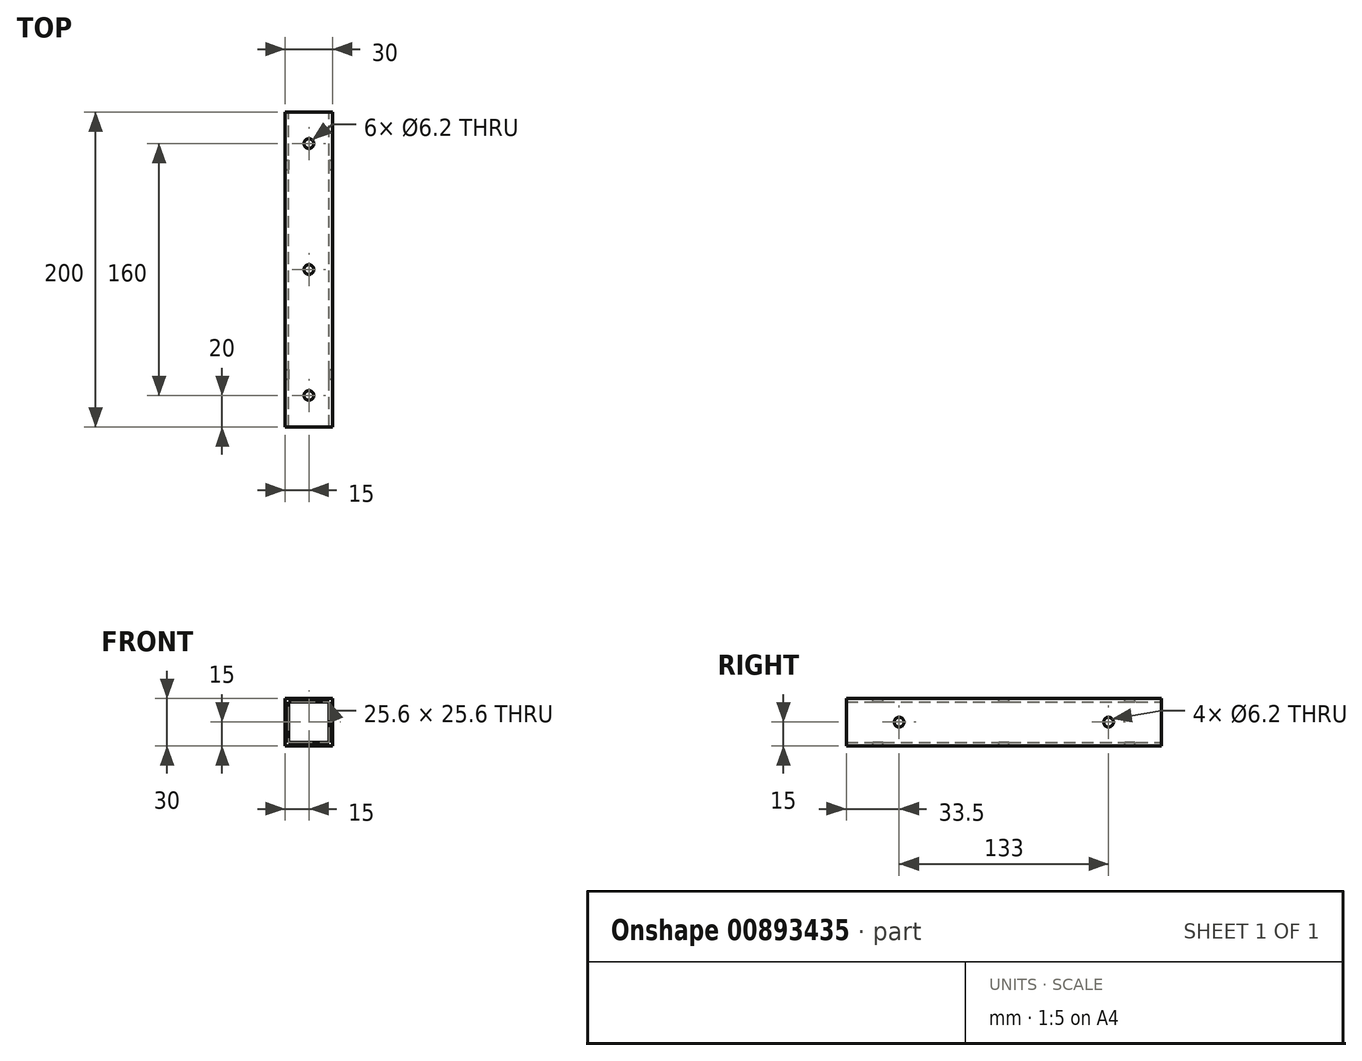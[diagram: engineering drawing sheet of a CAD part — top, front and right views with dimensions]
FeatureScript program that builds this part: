
annotation { "Feature Type Name" : "Feature", "Feature Type Description" : "" }
export const myFeature = defineFeature(function(context is Context, id is Id, definition is map)
    precondition{}
    {
        {
            var Q0;
            Q0=qCreatedBy(makeId("Front.planeOp"),FACE);
            var sketch = newSketch(context, id + "F0", { "sketchPlane" : qUnion([Q0])});
            skLineSegment(sketch, "E0.bottom", {"start": v(0, 0) * mm, "end": v(30, 0) * mm});
            skLineSegment(sketch, "E0.top", {"start": v(0, 30) * mm, "end": v(30, 30) * mm});
            skLineSegment(sketch, "E0.left", {"start": v(0, 0) * mm, "end": v(0, 30) * mm});
            skLineSegment(sketch, "E0.right", {"start": v(30, 0) * mm, "end": v(30, 30) * mm});
            skLineSegment(sketch, "E1.bottom", {"start": v(2.2, 27.8) * mm, "end": v(27.8, 27.8) * mm});
            skLineSegment(sketch, "E1.top", {"start": v(2.2, 2.2) * mm, "end": v(27.8, 2.2) * mm});
            skLineSegment(sketch, "E1.left", {"start": v(2.2, 27.8) * mm, "end": v(2.2, 2.2) * mm});
            skLineSegment(sketch, "E1.right", {"start": v(27.8, 27.8) * mm, "end": v(27.8, 2.2) * mm});
            skSolve(sketch);
        }
        {
            var Q0;
            Q0=makeQuery(id+"F0.imprint","IMPRINT",FACE,{"disambiguationData":[TD([[makeQuery(id+"F0.imprint","IMPRINT",EDGE,{"derivedFrom":sQuery(id+"F0.wireOp",EDGE,"E0.bottom")}),1.0]])]});
            extrude(context, id + "F1", {"entities" : qUnion([Q0]), "depth" : 200 * mm, "offsetDistance" : 25 * mm});
        }
        {
            var Q0;
            Q0=makeQuery(id+"F1.opExtrude","SWEPT_FACE",FACE,{"disambiguationData":[OSD([sQuery(id+"F0.wireOp",EDGE,"E0.top")])]});
            var sketch = newSketch(context, id + "F2", { "sketchPlane" : qUnion([Q0])});
            skCircle(sketch, "E2", {"center": v(15, -180) * mm, "radius": 3.1 * mm});
            skPoint(sketch, "E2.centerSnap0", {"position": v(15, -200) * mm});
            skCircle(sketch, "E3", {"center": v(15, -100) * mm, "radius": 3.1 * mm});
            skCircle(sketch, "E4", {"center": v(15, -20) * mm, "radius": 3.1 * mm});
            skSolve(sketch);
        }
        {
            var Q0;
            Q0=makeQuery(id+"F2.imprint","IMPRINT",FACE,{"disambiguationData":[TD([[makeQuery(id+"F2.imprint","IMPRINT",EDGE,{"derivedFrom":sQuery(id+"F2.wireOp",EDGE,"E4")}),1.0]])]});
            var Q1;
            Q1=makeQuery(id+"F2.imprint","IMPRINT",FACE,{"disambiguationData":[TD([[makeQuery(id+"F2.imprint","IMPRINT",EDGE,{"derivedFrom":sQuery(id+"F2.wireOp",EDGE,"E3")}),1.0]])]});
            var Q2;
            Q2=makeQuery(id+"F2.imprint","IMPRINT",FACE,{"disambiguationData":[TD([[makeQuery(id+"F2.imprint","IMPRINT",EDGE,{"derivedFrom":sQuery(id+"F2.wireOp",EDGE,"E2")}),1.0]])]});
            extrude(context, id + "F3", {"entities" : qUnion([Q0, Q1, Q2]), "operationType" : NewBodyOperationType.REMOVE, "oppositeDirection" : true, "depth" : 35 * mm, "offsetDistance" : 25 * mm});
        }
        {
            var Q0;
            Q0=makeQuery(id+"F1.opExtrude","SWEPT_FACE",FACE,{"disambiguationData":[OSD([sQuery(id+"F0.wireOp",EDGE,"E0.right")])]});
            var sketch = newSketch(context, id + "F4", { "sketchPlane" : qUnion([Q0])});
            skCircle(sketch, "E5", {"center": v(-166.5, 15) * mm, "radius": 3.1 * mm});
            skPoint(sketch, "E5.centerSnap0", {"position": v(-200, 15) * mm});
            skCircle(sketch, "E6", {"center": v(-33.5, 15) * mm, "radius": 3.1 * mm});
            skPoint(sketch, "E6.centerSnap0", {"position": v(0, 15) * mm});
            skSolve(sketch);
        }
        {
            var Q0;
            Q0=makeQuery(id+"F4.imprint","IMPRINT",FACE,{"disambiguationData":[TD([[makeQuery(id+"F4.imprint","IMPRINT",EDGE,{"derivedFrom":sQuery(id+"F4.wireOp",EDGE,"E5")}),1.0]])]});
            var Q1;
            Q1=makeQuery(id+"F4.imprint","IMPRINT",FACE,{"disambiguationData":[TD([[makeQuery(id+"F4.imprint","IMPRINT",EDGE,{"derivedFrom":sQuery(id+"F4.wireOp",EDGE,"E6")}),1.0]])]});
            extrude(context, id + "F5", {"entities" : qUnion([Q0, Q1]), "operationType" : NewBodyOperationType.REMOVE, "oppositeDirection" : true, "depth" : 35 * mm, "offsetDistance" : 25 * mm});
        }
    });
